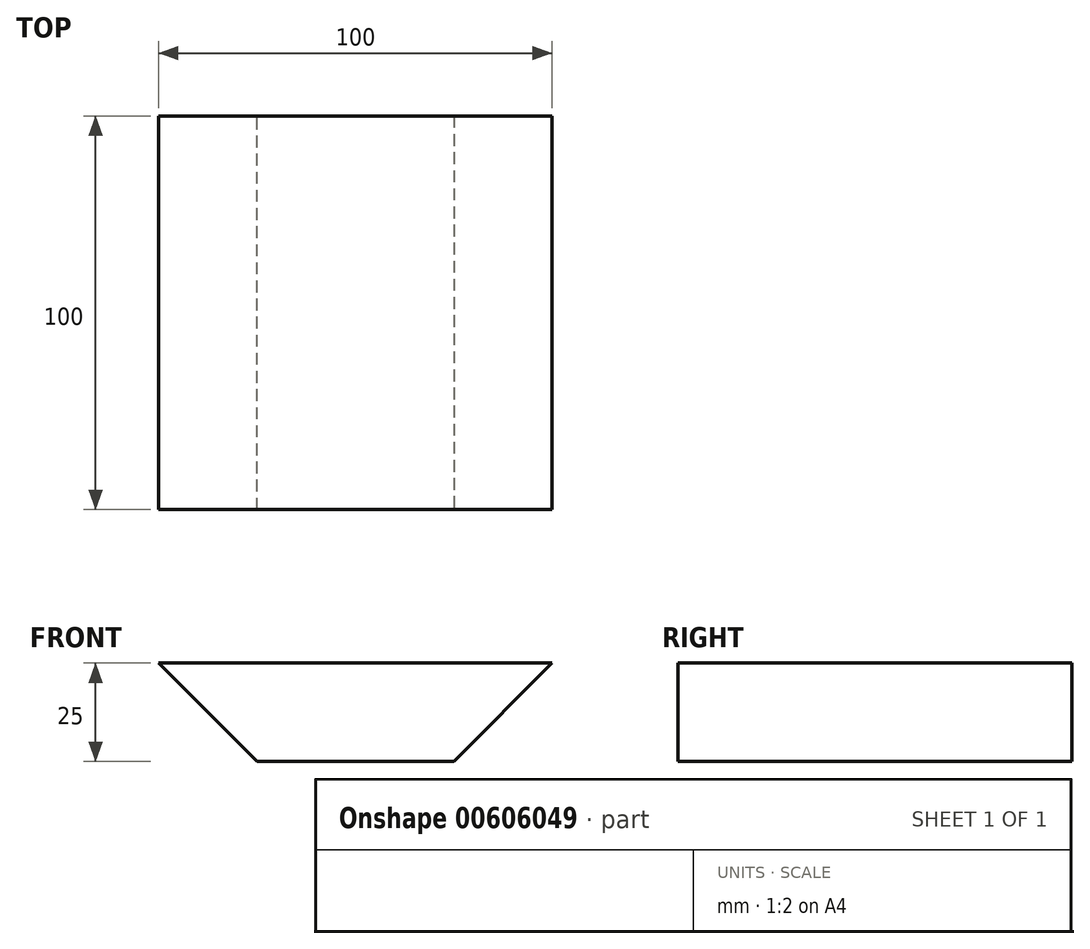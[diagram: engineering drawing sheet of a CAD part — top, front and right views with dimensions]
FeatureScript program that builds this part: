
annotation { "Feature Type Name" : "Feature", "Feature Type Description" : "" }
export const myFeature = defineFeature(function(context is Context, id is Id, definition is map)
    precondition{}
    {
        {
            var Q0;
            Q0=qCreatedBy(makeId("Top.planeOp"),FACE);
            var sketch = newSketch(context, id + "F0", { "sketchPlane" : qUnion([Q0])});
            skLineSegment(sketch, "E0.bottom", {"start": v(50, -50) * mm, "end": v(-50, -50) * mm});
            skLineSegment(sketch, "E0.top", {"start": v(50, 50) * mm, "end": v(-50, 50) * mm});
            skLineSegment(sketch, "E0.left", {"start": v(50, -50) * mm, "end": v(50, 50) * mm});
            skLineSegment(sketch, "E0.right", {"start": v(-50, -50) * mm, "end": v(-50, 50) * mm});
            skPoint(sketch, "E0.middle", {"position": v(0, 0) * mm});
            skSolve(sketch);
        }
        {
            var Q0;
            Q0 = qSketchRegion(id + "F0", true);
            var Q1;
            Q1=makeQuery(id+"F0.imprint","IMPRINT",FACE,{"disambiguationData":[TD([[makeQuery(id+"F0.imprint","IMPRINT",EDGE,{"derivedFrom":sQuery(id+"F0.wireOp",EDGE,"E0.bottom")}),-1.0]])]});
            extrude(context, id + "F1", {"entities" : qUnion([Q0, Q1]), "depth" : 25 * mm, "offsetDistance" : 25 * mm});
        }
        {
            var Q0;
            Q0=makeQuery(id+"F1.opExtrude","CAP_EDGE",EDGE,{"disambiguationData":[OSD([sQuery(id+"F0.wireOp",EDGE,"E0.left")])],"isStart":true});
            var Q1;
            Q1=makeQuery(id+"F1.opExtrude","CAP_EDGE",EDGE,{"disambiguationData":[OSD([sQuery(id+"F0.wireOp",EDGE,"E0.right")])],"isStart":true});
            chamfer(context, id + "F2", {"entities" : qUnion([Q0, Q1]), "width" : 25 * mm, "tangentPropagation" : true});
        }
    });
